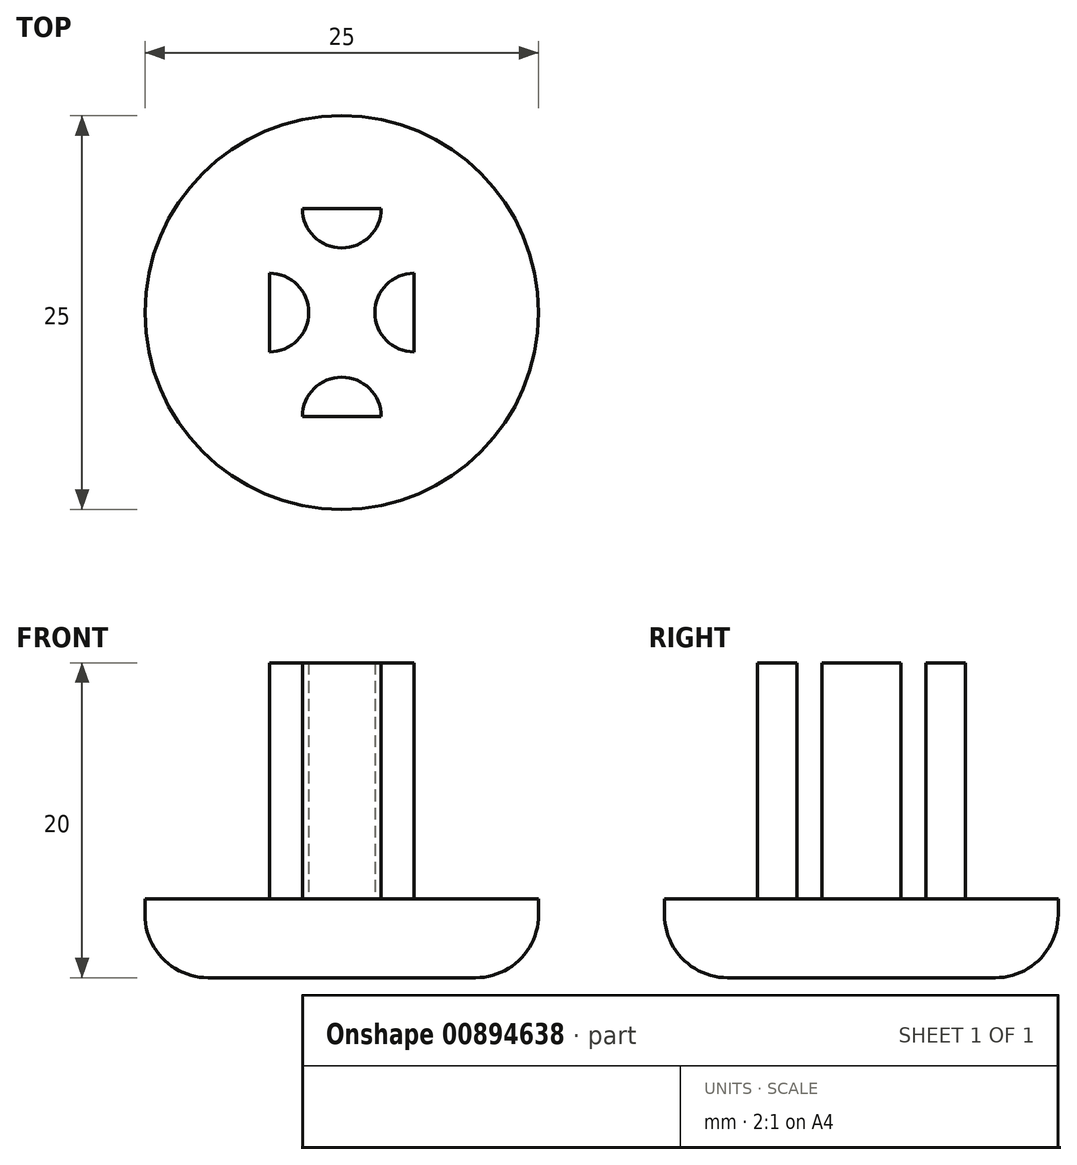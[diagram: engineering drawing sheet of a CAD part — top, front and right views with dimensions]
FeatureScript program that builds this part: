
annotation { "Feature Type Name" : "Feature", "Feature Type Description" : "" }
export const myFeature = defineFeature(function(context is Context, id is Id, definition is map)
    precondition{}
    {
        {
            var Q0;
            Q0=qCreatedBy(makeId("Top.planeOp"),FACE);
            var sketch = newSketch(context, id + "F0", { "sketchPlane" : qUnion([Q0])});
            skCircle(sketch, "E0", {"center": v(0, 0) * mm, "radius": 12.5 * mm});
            skPoint(sketch, "E1.orphan", {"position": v(4.6, -6.6) * mm});
            skPoint(sketch, "E2.orphan", {"position": v(-4.6, -6.6) * mm});
            skPoint(sketch, "E3.orphan", {"position": v(-4.6, 6.6) * mm});
            skSolve(sketch);
        }
        {
            var Q0;
            Q0=makeQuery(id+"F0.imprint","IMPRINT",FACE,{"disambiguationData":[TD([[makeQuery(id+"F0.imprint","IMPRINT",EDGE,{"derivedFrom":sQuery(id+"F0.wireOp",EDGE,"E0")}),1.0]])]});
            extrude(context, id + "F1", {"entities" : qUnion([Q0]), "depth" : 5 * mm, "offsetDistance" : 25 * mm});
        }
        {
            var Q0;
            Q0=makeQuery(id+"F1.opExtrude","CAP_EDGE",EDGE,{"disambiguationData":[OSD([sQuery(id+"F0.wireOp",EDGE,"E0")])],"isStart":true});
            fillet(context, id + "F2", {"entities" : qUnion([Q0]), "radius" : 4 * mm, "tangentPropagation" : true, "allowEdgeOverflow" : false});
        }
        {
            var Q0;
            Q0=makeQuery(id+"F1.opExtrude","CAP_FACE",FACE,{"disambiguationData":[OSD([sQuery(id+"F0.wireOp",EDGE,"E0")])],"isStart":false});
            var sketch = newSketch(context, id + "F3", { "sketchPlane" : qUnion([Q0])});
            skLineSegment(sketch, "E4.bottom", {"start": v(4.6, -6.6) * mm, "end": v(-4.6, -6.6) * mm});
            skLineSegment(sketch, "E4.top", {"start": v(4.6, 6.6) * mm, "end": v(-4.6, 6.6) * mm});
            skLineSegment(sketch, "E4.left", {"start": v(4.6, -6.6) * mm, "end": v(4.6, 6.6) * mm});
            skLineSegment(sketch, "E4.right", {"start": v(-4.6, -6.6) * mm, "end": v(-4.6, 6.6) * mm});
            skPoint(sketch, "E4.middle", {"position": v(0, 0) * mm});
            skCircle(sketch, "E5", {"center": v(0, 6.6) * mm, "radius": 2.5 * mm});
            skCircle(sketch, "E6", {"center": v(4.6, 0) * mm, "radius": 2.5 * mm});
            skCircle(sketch, "E7", {"center": v(0, -6.6) * mm, "radius": 2.5 * mm});
            skCircle(sketch, "E8", {"center": v(-4.6, 0) * mm, "radius": 2.5 * mm});
            skSolve(sketch);
        }
        {
            var Q0;
            {var subQ0=sQuery(id+"F3.wireOp",EDGE,"E7");var subQ1=sQuery(id+"F3.wireOp",EDGE,"E4.bottom");var subQ2=makeQuery(id+"F3.imprint","INTERSECT",VERTEX,{"disambiguationData":[OD(0.0)],"derivedFrom":[subQ1,subQ0]});Q0=makeQuery(id+"F3.imprint","IMPRINT",FACE,{"disambiguationData":[TD([[makeQuery(id+"F3.imprint","IMPRINT",EDGE,{"disambiguationData":[TD([[subQ2,-1.0]])],"derivedFrom":subQ1}),-1.0]])]});}
            var Q1;
            {var subQ0=sQuery(id+"F3.wireOp",EDGE,"E5");var subQ1=sQuery(id+"F3.wireOp",EDGE,"E4.top");var subQ2=makeQuery(id+"F3.imprint","INTERSECT",VERTEX,{"disambiguationData":[OD(0.0)],"derivedFrom":[subQ1,subQ0]});Q1=makeQuery(id+"F3.imprint","IMPRINT",FACE,{"disambiguationData":[TD([[makeQuery(id+"F3.imprint","IMPRINT",EDGE,{"disambiguationData":[TD([[subQ2,-1.0]])],"derivedFrom":subQ1}),1.0]])]});}
            var Q2;
            {var subQ0=sQuery(id+"F3.wireOp",EDGE,"E6");var subQ1=sQuery(id+"F3.wireOp",EDGE,"E4.left");var subQ2=makeQuery(id+"F3.imprint","INTERSECT",VERTEX,{"disambiguationData":[OD(0.0)],"derivedFrom":[subQ1,subQ0]});Q2=makeQuery(id+"F3.imprint","IMPRINT",FACE,{"disambiguationData":[TD([[makeQuery(id+"F3.imprint","IMPRINT",EDGE,{"disambiguationData":[TD([[subQ2,-1.0]])],"derivedFrom":subQ1}),1.0]])]});}
            var Q3;
            {var subQ0=sQuery(id+"F3.wireOp",EDGE,"E8");var subQ1=sQuery(id+"F3.wireOp",EDGE,"E4.right");var subQ2=makeQuery(id+"F3.imprint","INTERSECT",VERTEX,{"disambiguationData":[OD(0.0)],"derivedFrom":[subQ1,subQ0]});Q3=makeQuery(id+"F3.imprint","IMPRINT",FACE,{"disambiguationData":[TD([[makeQuery(id+"F3.imprint","IMPRINT",EDGE,{"disambiguationData":[TD([[subQ2,-1.0]])],"derivedFrom":subQ1}),-1.0]])]});}
            extrude(context, id + "F4", {"entities" : qUnion([Q0, Q1, Q2, Q3]), "operationType" : NewBodyOperationType.ADD, "depth" : 15 * mm, "offsetDistance" : 25 * mm});
        }
    });
